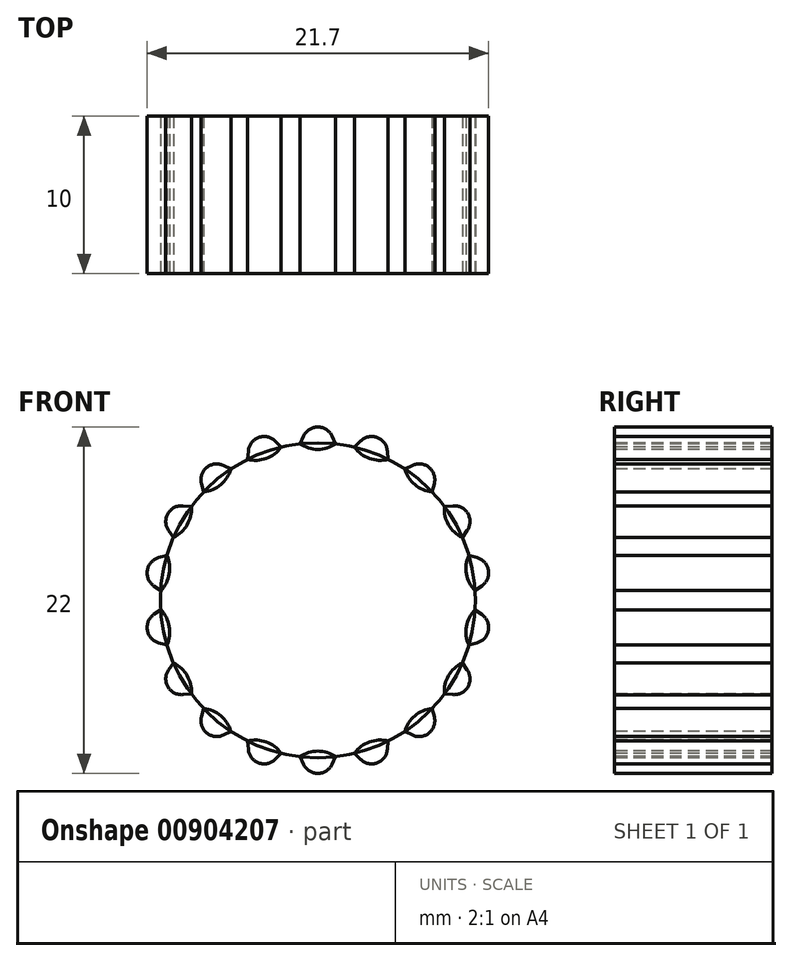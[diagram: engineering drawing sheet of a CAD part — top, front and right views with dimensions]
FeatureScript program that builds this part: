
annotation { "Feature Type Name" : "Feature", "Feature Type Description" : "" }
export const myFeature = defineFeature(function(context is Context, id is Id, definition is map)
    precondition{}
    {
        {
            var Q0;
            Q0=qCreatedBy(makeId("Front.planeOp"),FACE);
            var sketch = newSketch(context, id + "F0", { "sketchPlane" : qUnion([Q0])});
            skLineSegment(sketch, "E0", {"start": v(0, 43.53) * mm, "end": v(0, -35.67) * mm, "construction": true});
            skLineSegment(sketch, "E1", {"start": v(-16.98, 0) * mm, "end": v(15.77, 0) * mm, "construction": true});
            skCircle(sketch, "E2", {"center": v(0, 0) * mm, "radius": 10 * mm});
            skArc(sketch, "E3", {"start": v(0, 11) * mm, "mid": v(-0.54, 10.84) * mm, "end": v(-0.9, 10.42) * mm});
            skLineSegment(sketch, "E4", {"start": v(-1.13, 9.94) * mm, "end": v(-0.9, 10.42) * mm});
            skLineSegment(sketch, "E5.MirrorCS", {"start": v(1.13, 9.94) * mm, "end": v(0.9, 10.42) * mm});
            skArc(sketch, "E6.MirrorCS", {"start": v(0, 11) * mm, "mid": v(0.54, 10.84) * mm, "end": v(0.9, 10.42) * mm});
            skSolve(sketch);
        }
        {
            var Q0;
            {var subQ0=sQuery(id+"F0.wireOp",EDGE,"E2");var subQ1=makeQuery(id+"F0.imprint","INTERSECT",VERTEX,{"derivedFrom":[subQ0,sQuery(id+"F0.wireOp",EDGE,"E4")]});Q0=makeQuery(id+"F0.imprint","IMPRINT",FACE,{"disambiguationData":[TD([[makeQuery(id+"F0.imprint","IMPRINT",EDGE,{"disambiguationData":[TD([[subQ1,1.0]])],"derivedFrom":subQ0}),1.0]])]});}
            extrude(context, id + "F1", {"entities" : qUnion([Q0]), "oppositeDirection" : true, "depth" : 10 * mm, "offsetDistance" : 25 * mm});
        }
        {
            var Q0;
            {var subQ0=sQuery(id+"F0.wireOp",EDGE,"E2");var subQ1=makeQuery(id+"F0.imprint","INTERSECT",VERTEX,{"derivedFrom":[subQ0,sQuery(id+"F0.wireOp",EDGE,"E4")]});Q0=makeQuery(id+"F0.imprint","IMPRINT",FACE,{"disambiguationData":[TD([[makeQuery(id+"F0.imprint","IMPRINT",EDGE,{"disambiguationData":[TD([[subQ1,1.0]])],"derivedFrom":subQ0}),1.0]])]});}
            var sketch = newSketch(context, id + "F2", { "sketchPlane" : qUnion([Q0])});
            skLineSegment(sketch, "E7.0", {"start": v(-1.13, 9.94) * mm, "end": v(-0.9, 10.42) * mm});
            skArc(sketch, "E7.1", {"start": v(0, 11) * mm, "mid": v(-0.54, 10.84) * mm, "end": v(-0.9, 10.42) * mm});
            skArc(sketch, "E7.2", {"start": v(0, 11) * mm, "mid": v(0.54, 10.84) * mm, "end": v(0.9, 10.42) * mm});
            skLineSegment(sketch, "E7.3", {"start": v(1.13, 9.94) * mm, "end": v(0.9, 10.42) * mm});
            skArc(sketch, "E8", {"start": v(-1.13, 9.94) * mm, "mid": v(0, 9.58) * mm, "end": v(1.13, 9.94) * mm});
            skSolve(sketch);
        }
        {
            var Q0;
            Q0 = qSketchRegion(id + "F2", true);
            extrude(context, id + "F3", {"entities" : qUnion([Q0]), "oppositeDirection" : true, "depth" : 10 * mm, "offsetDistance" : 25 * mm});
        }
        {
            var Q0;
            Q0=makeQuery(id+"F3.opExtrude","SWEPT_BODY",BODY,{"disambiguationData":[OSD([sQuery(id+"F2.wireOp",EDGE,"E7.0"),sQuery(id+"F2.wireOp",EDGE,"E7.1"),sQuery(id+"F2.wireOp",EDGE,"E7.2"),sQuery(id+"F2.wireOp",EDGE,"E7.3"),sQuery(id+"F2.wireOp",EDGE,"E8")])]});
            var Q1;
            Q1=makeQuery(id+"F1.opExtrude","SWEPT_FACE",FACE,{"disambiguationData":[OSD([sQuery(id+"F0.wireOp",EDGE,"E2")])]});
            circularPattern(context, id + "F4", {"entities" : qUnion([Q0]), "axis" : qUnion([Q1]), "angle" : 360 * degree, "instanceCount" : 18, "equalSpace" : true});
        }
    });
